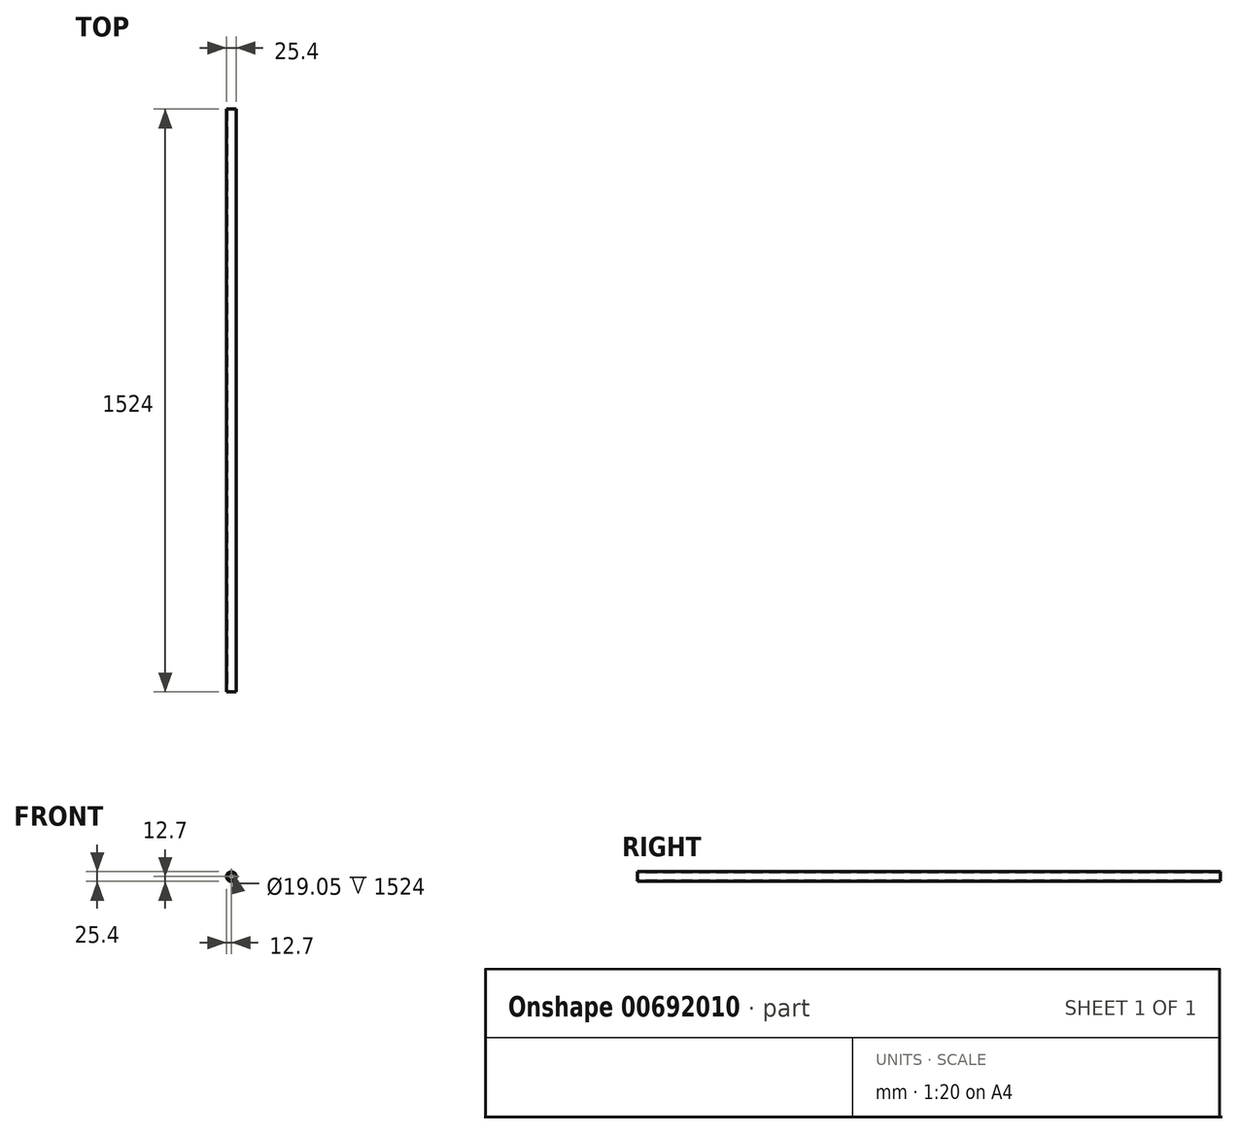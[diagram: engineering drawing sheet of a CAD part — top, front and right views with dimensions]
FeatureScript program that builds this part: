
annotation { "Feature Type Name" : "Feature", "Feature Type Description" : "" }
export const myFeature = defineFeature(function(context is Context, id is Id, definition is map)
    precondition{}
    {
        {
            var Q0;
            Q0=qCreatedBy(makeId("Front.planeOp"),FACE);
            var sketch = newSketch(context, id + "F0", { "sketchPlane" : qUnion([Q0])});
            skCircle(sketch, "E0", {"center": v(0, 0) * mm, "radius": 12.7 * mm});
            skSolve(sketch);
        }
        {
            var Q0;
            Q0 = qSketchRegion(id + "F0", true);
            extrude(context, id + "F1", {"entities" : qUnion([Q0]), "depth" : 1524 * mm, "offsetDistance" : 25.4 * mm});
        }
        {
            var Q0;
            Q0=makeQuery(id+"F1.opExtrude","CAP_FACE",FACE,{"disambiguationData":[OSD([sQuery(id+"F0.wireOp",EDGE,"E0")])],"isStart":false});
            var sketch = newSketch(context, id + "F2", { "sketchPlane" : qUnion([Q0])});
            skCircle(sketch, "E1", {"center": v(0, 0) * mm, "radius": 9.53 * mm});
            skSolve(sketch);
        }
        {
            var Q0;
            Q0=makeQuery(id+"F2.imprint","IMPRINT",FACE,{"disambiguationData":[TD([[makeQuery(id+"F2.imprint","IMPRINT",EDGE,{"derivedFrom":sQuery(id+"F2.wireOp",EDGE,"E1")}),1.0]])]});
            extrude(context, id + "F3", {"entities" : qUnion([Q0]), "operationType" : NewBodyOperationType.REMOVE, "endBound" : BoundingType.THROUGH_ALL, "oppositeDirection" : true, "depth" : 25.4 * mm, "offsetDistance" : 25.4 * mm});
        }
    });
